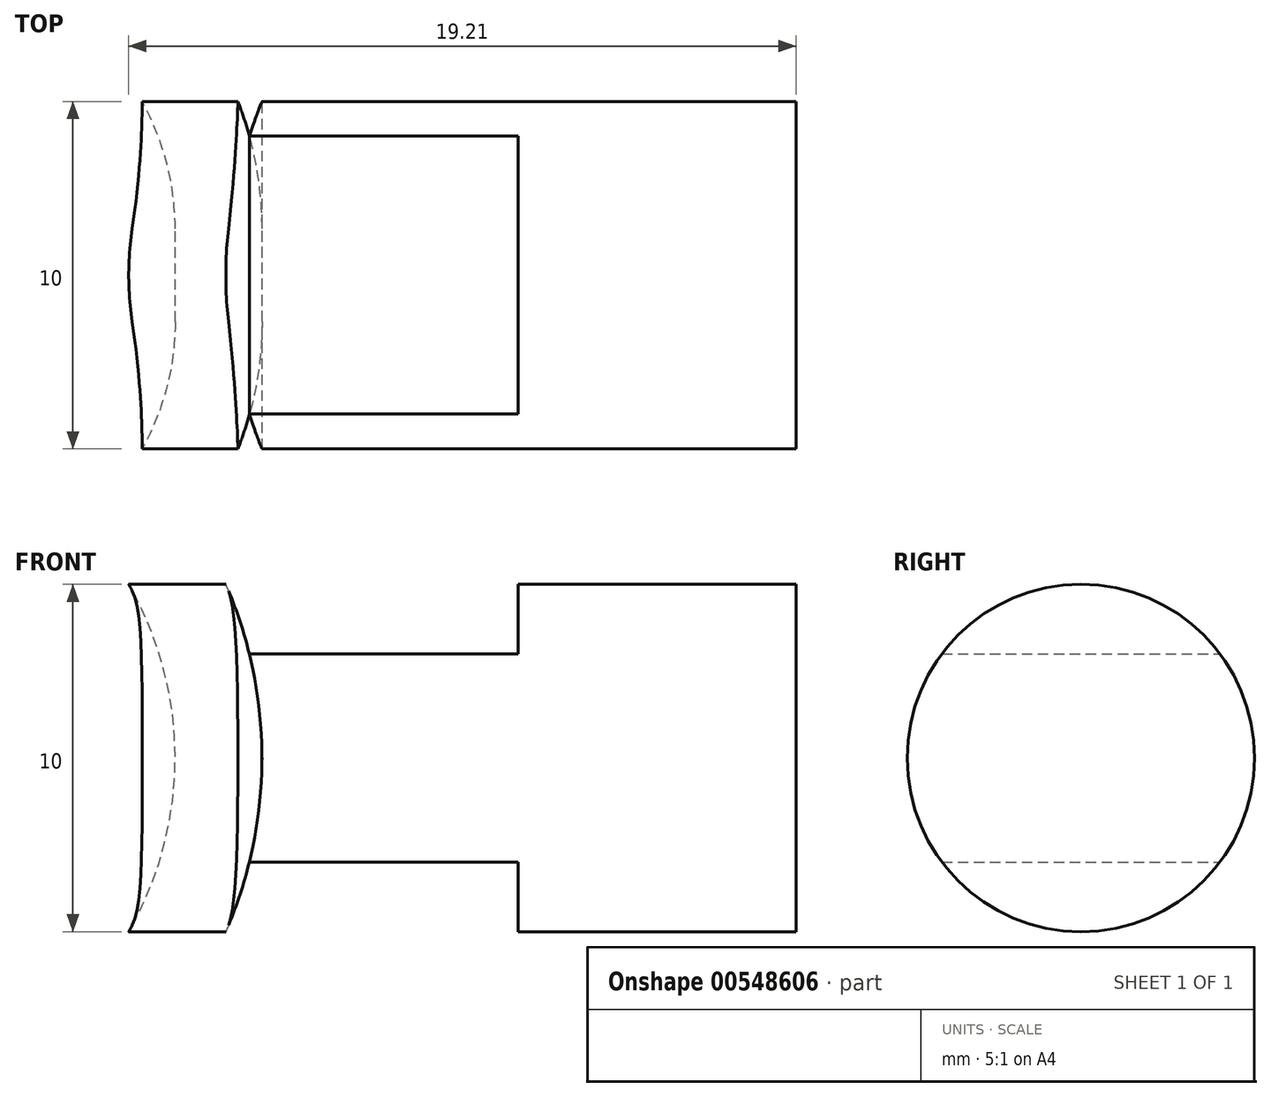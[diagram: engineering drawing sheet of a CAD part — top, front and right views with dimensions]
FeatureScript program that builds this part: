
annotation { "Feature Type Name" : "Feature", "Feature Type Description" : "" }
export const myFeature = defineFeature(function(context is Context, id is Id, definition is map)
    precondition{}
    {
        {
            var Q0;
            Q0=qCreatedBy(makeId("Front.planeOp"),FACE);
            var sketch = newSketch(context, id + "F0", { "sketchPlane" : qUnion([Q0])});
            skCircle(sketch, "E0", {"center": v(0, 0) * mm, "radius": 12.5 * mm});
            skCircle(sketch, "E1", {"center": v(0, 0) * mm, "radius": 7.5 * mm});
            skLineSegment(sketch, "E2", {"start": v(12.13, 3) * mm, "end": v(19.87, 3) * mm});
            skLineSegment(sketch, "E3", {"start": v(19.87, 3) * mm, "end": v(19.87, 5) * mm});
            skLineSegment(sketch, "E4", {"start": v(19.87, 5) * mm, "end": v(27.87, 5) * mm});
            skLineSegment(sketch, "E5", {"start": v(0, 0) * mm, "end": v(31.52, 0) * mm, "construction": true});
            skLineSegment(sketch, "E6.MirrorCS", {"start": v(12.13, -3) * mm, "end": v(19.87, -3) * mm});
            skLineSegment(sketch, "E7.MirrorCS", {"start": v(19.87, -5) * mm, "end": v(27.87, -5) * mm});
            skLineSegment(sketch, "E8.MirrorCS", {"start": v(19.87, -3) * mm, "end": v(19.87, -5) * mm});
            skPoint(sketch, "E9.orphan", {"position": v(6.87, 3) * mm});
            skPoint(sketch, "E10.orphan", {"position": v(6.87, -3) * mm});
            skLineSegment(sketch, "E11", {"start": v(27.87, 5) * mm, "end": v(27.87, -5) * mm});
            skSolve(sketch);
        }
        {
            var Q0;
            Q0=makeQuery(id+"F0.imprint","IMPRINT",FACE,{"disambiguationData":[TD([[makeQuery(id+"F0.imprint","IMPRINT",EDGE,{"derivedFrom":sQuery(id+"F0.wireOp",EDGE,"E0")}),1.0]])]});
            extrude(context, id + "F1", {"entities" : qUnion([Q0]), "endBound" : BoundingType.SYMMETRIC, "depth" : 20 * mm, "offsetDistance" : 25 * mm});
        }
        {
            var Q0;
            Q0=makeQuery(id+"F1.opExtrude","CAP_EDGE",EDGE,{"disambiguationData":[OSD([sQuery(id+"F0.wireOp",EDGE,"E0")])],"isStart":false});
            var Q1;
            Q1=makeQuery(id+"F1.opExtrude","CAP_EDGE",EDGE,{"disambiguationData":[OSD([sQuery(id+"F0.wireOp",EDGE,"E0")])],"isStart":true});
            fillet(context, id + "F2", {"entities" : qUnion([Q0, Q1]), "radius" : 10 * mm, "tangentPropagation" : true, "allowEdgeOverflow" : false});
        }
        {
            var Q0;
            Q0=makeQuery(id+"F1.opExtrude","SWEPT_FACE",FACE,{"disambiguationData":[OSD([sQuery(id+"F0.wireOp",EDGE,"E1")])]});
            shell(context, id + "F3", {"entities" : qUnion([Q0]), "thickness" : 2.5 * mm});
        }
        {
            var Q0;
            {var subQ0=sQuery(id+"F0.wireOp",EDGE,"E2");Q0=makeQuery(id+"F0.imprint","IMPRINT",FACE,{"disambiguationData":[TD([[makeQuery(id+"F0.imprint","IMPRINT",EDGE,{"derivedFrom":subQ0}),-1.0]])]});}
            extrude(context, id + "F4", {"entities" : qUnion([Q0]), "endBound" : BoundingType.SYMMETRIC, "depth" : 10 * mm, "offsetDistance" : 25 * mm});
        }
        {
            var Q0;
            Q0=makeQuery(id+"F4.opExtrude","SWEPT_FACE",FACE,{"disambiguationData":[OSD([sQuery(id+"F0.wireOp",EDGE,"E11")])]});
            var sketch = newSketch(context, id + "F5", { "sketchPlane" : qUnion([Q0])});
            skCircle(sketch, "E12", {"center": v(0, 0) * mm, "radius": 5 * mm});
            skSolve(sketch);
        }
        {
            var Q0;
            {var subQ0=sQuery(id+"F5.wireOp",EDGE,"E12");var subQ1=sQuery(id+"F0.wireOp",EDGE,"E11");var subQ3=makeQuery(id+"F5.imprint","INTERSECT",VERTEX,{"derivedFrom":[makeQuery(id+"F4.opExtrude","CAP_EDGE",EDGE,{"disambiguationData":[OSD([subQ1])],"isStart":true}),subQ0]});Q0=makeQuery(id+"F5.imprint","IMPRINT",FACE,{"disambiguationData":[TD([[makeQuery(id+"F5.imprint","IMPRINT",EDGE,{"disambiguationData":[TD([[subQ3,-1.0]])],"derivedFrom":subQ0}),1.0]])]});}
            extrude(context, id + "F6", {"entities" : qUnion([Q0]), "operationType" : NewBodyOperationType.INTERSECT, "oppositeDirection" : true, "depth" : 25 * mm, "offsetDistance" : 25 * mm});
        }
    });
